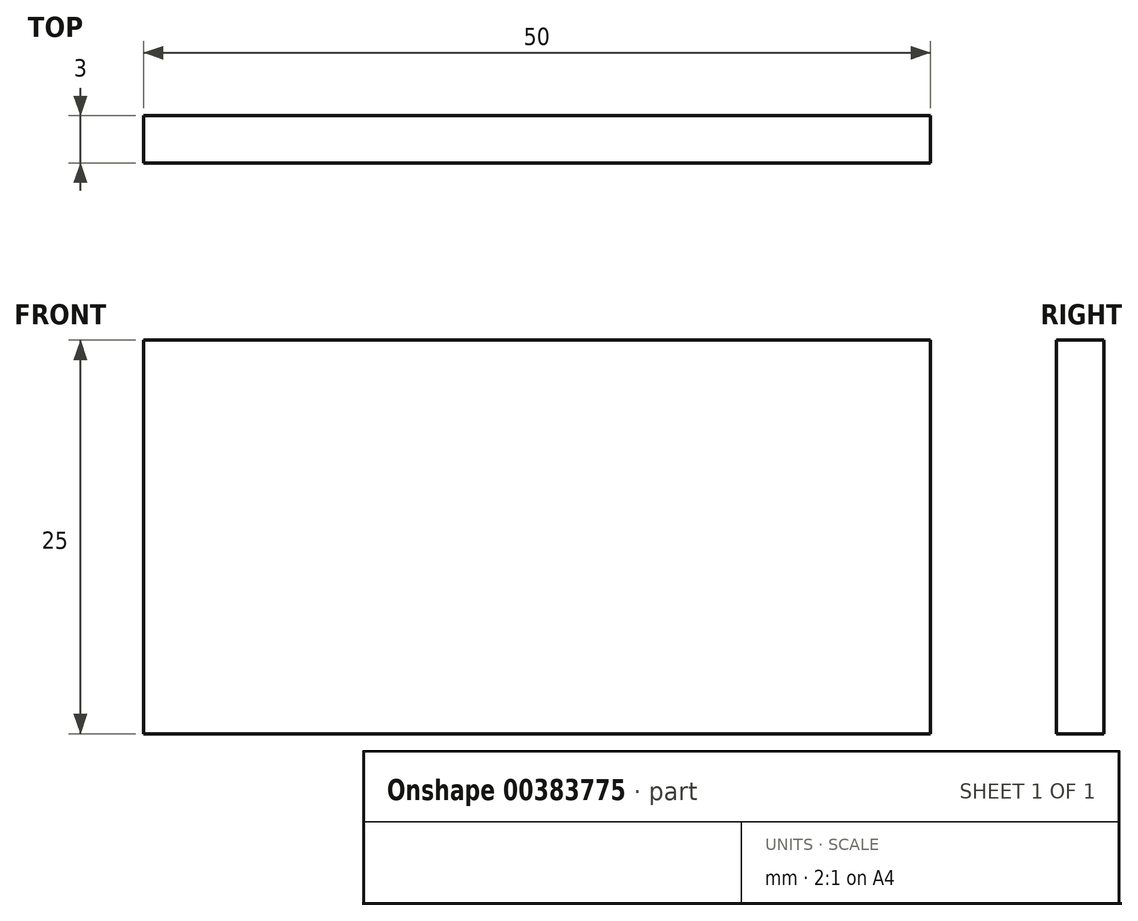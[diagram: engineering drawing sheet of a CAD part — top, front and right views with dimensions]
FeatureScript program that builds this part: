
annotation { "Feature Type Name" : "Feature", "Feature Type Description" : "" }
export const myFeature = defineFeature(function(context is Context, id is Id, definition is map)
    precondition{}
    {
        {
            var Q0;
            Q0=qCreatedBy(makeId("Front.planeOp"),FACE);
            var sketch = newSketch(context, id + "F0", { "sketchPlane" : qUnion([Q0])});
            skLineSegment(sketch, "E0.bottom", {"start": v(-25, 12.5) * mm, "end": v(25, 12.5) * mm});
            skLineSegment(sketch, "E0.top", {"start": v(-25, -12.5) * mm, "end": v(25, -12.5) * mm});
            skLineSegment(sketch, "E0.left", {"start": v(-25, 12.5) * mm, "end": v(-25, -12.5) * mm});
            skLineSegment(sketch, "E0.right", {"start": v(25, 12.5) * mm, "end": v(25, -12.5) * mm});
            skPoint(sketch, "E0.middle", {"position": v(0, 0) * mm});
            skSolve(sketch);
        }
        {
            var Q0;
            Q0=makeQuery(id+"F0.imprint","IMPRINT",FACE,{"disambiguationData":[TD([[makeQuery(id+"F0.imprint","IMPRINT",EDGE,{"derivedFrom":sQuery(id+"F0.wireOp",EDGE,"E0.bottom")}),-1.0]])]});
            extrude(context, id + "F1", {"entities" : qUnion([Q0]), "oppositeDirection" : true, "depth" : 3 * mm});
        }
    });
